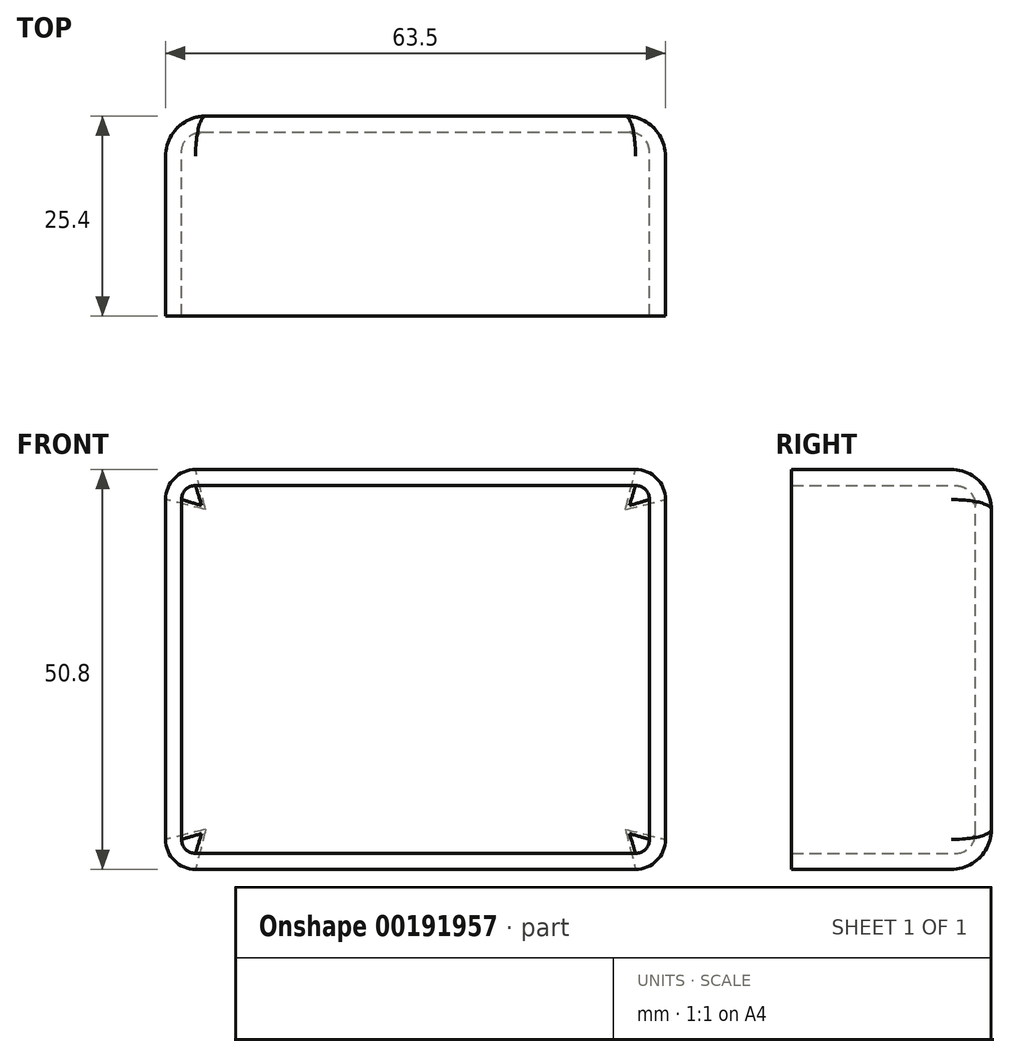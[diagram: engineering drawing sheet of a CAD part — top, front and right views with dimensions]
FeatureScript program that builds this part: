
annotation { "Feature Type Name" : "Feature", "Feature Type Description" : "" }
export const myFeature = defineFeature(function(context is Context, id is Id, definition is map)
    precondition{}
    {
        {
            var Q0;
            Q0=qCreatedBy(makeId("Front.planeOp"),FACE);
            var sketch = newSketch(context, id + "F0", { "sketchPlane" : qUnion([Q0])});
            skLineSegment(sketch, "E0", {"start": v(0, 0) * mm, "end": v(70.56, 0) * mm, "construction": true});
            skLineSegment(sketch, "E1", {"start": v(0, 0) * mm, "end": v(0, 21.59) * mm});
            skLineSegment(sketch, "E2", {"start": v(3.81, 25.4) * mm, "end": v(59.7, 25.4) * mm});
            skLineSegment(sketch, "E3", {"start": v(63.5, 21.59) * mm, "end": v(63.5, 0) * mm});
            skLineSegment(sketch, "E4.MirrorCS", {"start": v(0, 0) * mm, "end": v(0, -21.59) * mm});
            skLineSegment(sketch, "E5.MirrorCS", {"start": v(3.81, -25.4) * mm, "end": v(59.7, -25.4) * mm});
            skLineSegment(sketch, "E6.MirrorCS", {"start": v(63.5, -21.59) * mm, "end": v(63.5, 0) * mm});
            skPoint(sketch, "E7.visualSharp", {"position": v(0, 25.4) * mm});
            skArc(sketch, "E7.filletArc", {"start": v(3.81, 25.4) * mm, "mid": v(1.12, 24.28) * mm, "end": v(0, 21.59) * mm});
            skPoint(sketch, "E8.visualSharp", {"position": v(63.5, 25.4) * mm});
            skArc(sketch, "E8.filletArc", {"start": v(63.5, 21.59) * mm, "mid": v(62.38, 24.28) * mm, "end": v(59.7, 25.4) * mm});
            skPoint(sketch, "E9.visualSharp", {"position": v(63.5, -25.4) * mm});
            skArc(sketch, "E9.filletArc", {"start": v(59.7, -25.4) * mm, "mid": v(62.38, -24.28) * mm, "end": v(63.5, -21.59) * mm});
            skPoint(sketch, "E10.visualSharp", {"position": v(0, -25.4) * mm});
            skArc(sketch, "E10.filletArc", {"start": v(0, -21.59) * mm, "mid": v(1.12, -24.28) * mm, "end": v(3.81, -25.4) * mm});
            skSolve(sketch);
        }
        {
            var Q0;
            Q0=makeQuery(id+"F0.imprint","IMPRINT",FACE,{"disambiguationData":[TD([[makeQuery(id+"F0.imprint","IMPRINT",EDGE,{"derivedFrom":sQuery(id+"F0.wireOp",EDGE,"E1")}),-1.0]])]});
            extrude(context, id + "F1", {"entities" : qUnion([Q0]), "depth" : 25.4 * mm});
        }
        {
            var Q0;
            Q0=makeQuery(id+"F1.opExtrude","CAP_FACE",FACE,{"disambiguationData":[OSD([sQuery(id+"F0.wireOp",EDGE,"E1"),sQuery(id+"F0.wireOp",EDGE,"E2"),sQuery(id+"F0.wireOp",EDGE,"E3"),sQuery(id+"F0.wireOp",EDGE,"E4.MirrorCS"),sQuery(id+"F0.wireOp",EDGE,"E5.MirrorCS"),sQuery(id+"F0.wireOp",EDGE,"E6.MirrorCS")])],"isStart":false});
            shell(context, id + "F2", {"entities" : qUnion([Q0]), "thickness" : 2.03 * mm});
        }
        {
            var Q0;
            Q0=makeQuery(id+"F2.opShell","OFFSET_FACE",FACE,{"disambiguationData":[OSD([sQuery(id+"F0.wireOp",EDGE,"E1"),sQuery(id+"F0.wireOp",EDGE,"E2"),sQuery(id+"F0.wireOp",EDGE,"E3"),sQuery(id+"F0.wireOp",EDGE,"E4.MirrorCS"),sQuery(id+"F0.wireOp",EDGE,"E5.MirrorCS"),sQuery(id+"F0.wireOp",EDGE,"E6.MirrorCS"),sQuery(id+"F0.wireOp",EDGE,"E7.filletArc"),sQuery(id+"F0.wireOp",EDGE,"E8.filletArc"),sQuery(id+"F0.wireOp",EDGE,"E9.filletArc"),sQuery(id+"F0.wireOp",EDGE,"E10.filletArc")])]});
            fillet(context, id + "F3", {"entities" : qUnion([Q0]), "radius" : 2.54 * mm, "tangentPropagation" : true, "allowEdgeOverflow" : false});
        }
        {
            var Q0;
            Q0=makeQuery(id+"F1.opExtrude","CAP_FACE",FACE,{"disambiguationData":[OSD([sQuery(id+"F0.wireOp",EDGE,"E1"),sQuery(id+"F0.wireOp",EDGE,"E2"),sQuery(id+"F0.wireOp",EDGE,"E3"),sQuery(id+"F0.wireOp",EDGE,"E4.MirrorCS"),sQuery(id+"F0.wireOp",EDGE,"E5.MirrorCS"),sQuery(id+"F0.wireOp",EDGE,"E6.MirrorCS"),sQuery(id+"F0.wireOp",EDGE,"E7.filletArc"),sQuery(id+"F0.wireOp",EDGE,"E8.filletArc"),sQuery(id+"F0.wireOp",EDGE,"E9.filletArc"),sQuery(id+"F0.wireOp",EDGE,"E10.filletArc")])],"isStart":true});
            fillet(context, id + "F4", {"entities" : qUnion([Q0]), "radius" : 5.08 * mm, "tangentPropagation" : true, "allowEdgeOverflow" : false});
        }
    });
